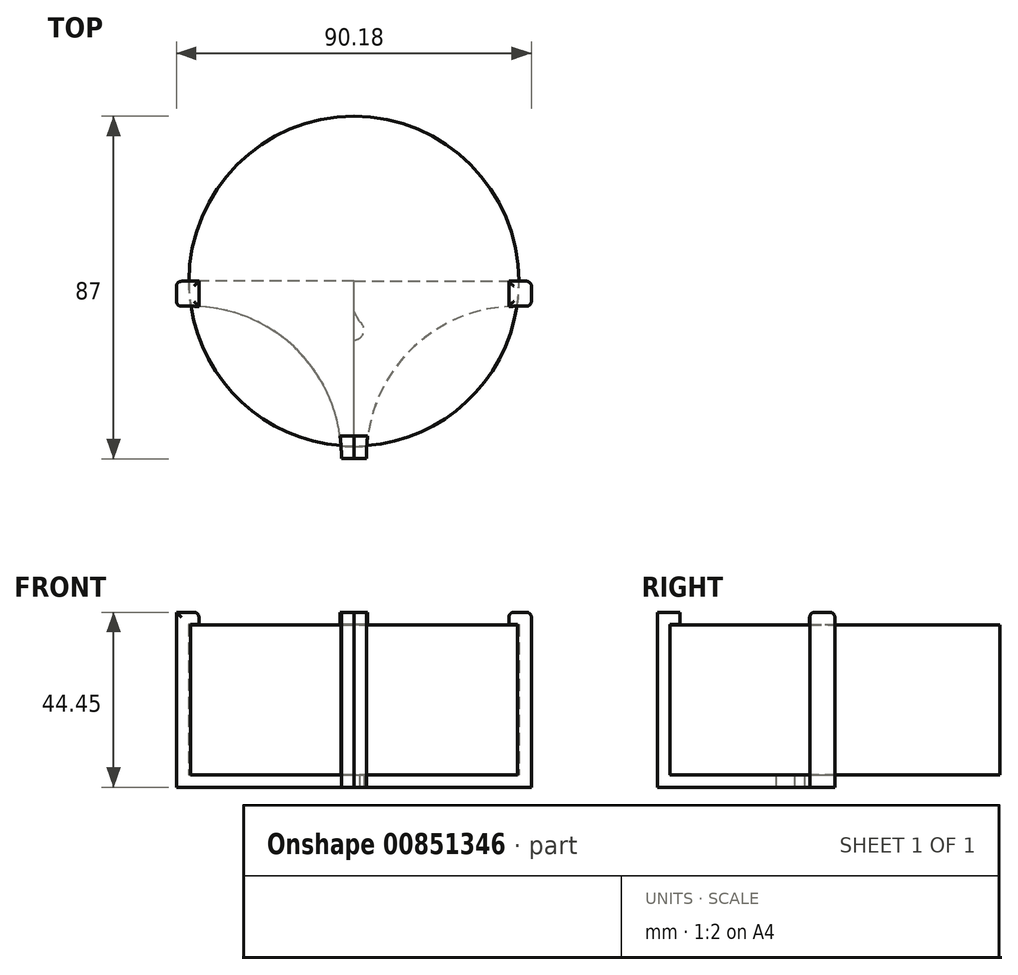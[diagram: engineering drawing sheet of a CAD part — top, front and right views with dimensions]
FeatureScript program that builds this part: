
annotation { "Feature Type Name" : "Feature", "Feature Type Description" : "" }
export const myFeature = defineFeature(function(context is Context, id is Id, definition is map)
    precondition{}
    {
        {
            var Q0;
            Q0=qCreatedBy(makeId("Top.planeOp"),FACE);
            var sketch = newSketch(context, id + "F0", { "sketchPlane" : qUnion([Q0])});
            skCircle(sketch, "E0", {"center": v(0, 0) * mm, "radius": 41.91 * mm});
            skSolve(sketch);
        }
        {
            var Q0;
            Q0=makeQuery(id+"F0.imprint","IMPRINT",FACE,{"disambiguationData":[TD([[makeQuery(id+"F0.imprint","IMPRINT",EDGE,{"derivedFrom":sQuery(id+"F0.wireOp",EDGE,"E0")}),1.0]])]});
            extrude(context, id + "F1", {"entities" : qUnion([Q0]), "depth" : 38.1 * mm, "offsetDistance" : 25.4 * mm});
        }
        {
            var Q0;
            Q0=qCreatedBy(makeId("Top.planeOp"),FACE);
            var sketch = newSketch(context, id + "F2", { "sketchPlane" : qUnion([Q0])});
            skLineSegment(sketch, "E1", {"start": v(0, 0) * mm, "end": v(45.09, 0) * mm});
            skLineSegment(sketch, "E2", {"start": v(45.09, 0) * mm, "end": v(45.09, -6.35) * mm});
            skLineSegment(sketch, "E3", {"start": v(45.08, -6.35) * mm, "end": v(41.27, -6.35) * mm});
            skLineSegment(sketch, "E4", {"start": v(3.18, -44.45) * mm, "end": v(3.18, -45.09) * mm});
            skLineSegment(sketch, "E5", {"start": v(3.18, -45.09) * mm, "end": v(0, -45.09) * mm});
            skLineSegment(sketch, "E6", {"start": v(0, -45.09) * mm, "end": v(0, 0) * mm});
            skPoint(sketch, "E7.visualSharp", {"position": v(3.17, -6.35) * mm});
            skArc(sketch, "E7.filletArc", {"start": v(41.27, -6.35) * mm, "mid": v(14.33, -17.5) * mm, "end": v(3.18, -44.45) * mm});
            skSolve(sketch);
        }
        {
            var Q0;
            Q0=makeQuery(id+"F2.imprint","IMPRINT",FACE,{"disambiguationData":[TD([[makeQuery(id+"F2.imprint","IMPRINT",EDGE,{"derivedFrom":sQuery(id+"F2.wireOp",EDGE,"E1")}),-1.0]])]});
            extrude(context, id + "F3", {"entities" : qUnion([Q0]), "depth" : 41.27 * mm, "offsetDistance" : 25.4 * mm, "hasSecondDirection" : true, "secondDirectionOppositeDirection" : true, "secondDirectionDepth" : 3.17 * mm});
        }
        {
            var Q0;
            Q0=makeQuery(id+"F1.opExtrude","SWEPT_BODY",BODY,{"disambiguationData":[OSD([sQuery(id+"F0.wireOp",EDGE,"E0")])]});
            var Q1;
            Q1=makeQuery(id+"F3.opExtrude","SWEPT_BODY",BODY,{"disambiguationData":[OSD([sQuery(id+"F2.wireOp",EDGE,"E1"),sQuery(id+"F2.wireOp",EDGE,"E2"),sQuery(id+"F2.wireOp",EDGE,"E3"),sQuery(id+"F2.wireOp",EDGE,"E4"),sQuery(id+"F2.wireOp",EDGE,"E5"),sQuery(id+"F2.wireOp",EDGE,"E6"),sQuery(id+"F2.wireOp",EDGE,"E7.filletArc")])]});
            var Q2;
            Q2=makeQuery(id+"F1.opExtrude","CAP_FACE",FACE,{"disambiguationData":[OSD([sQuery(id+"F0.wireOp",EDGE,"E0")])],"isStart":false});
            var Q3;
            Q3=makeQuery(id+"F1.opExtrude","SWEPT_FACE",FACE,{"disambiguationData":[OSD([sQuery(id+"F0.wireOp",EDGE,"E0")])]});
            var Q4;
            Q4=makeQuery(id+"F1.opExtrude","CAP_FACE",FACE,{"disambiguationData":[OSD([sQuery(id+"F0.wireOp",EDGE,"E0")])],"isStart":true});
            booleanBodies(context, id + "F4", {"operationType" : BooleanOperationType.SUBTRACTION, "tools" : qUnion([Q0]), "targets" : qUnion([Q1]), "offset" : true, "entitiesToOffset" : qUnion([Q2, Q3, Q4]), "offsetDistance" : 0.08 * mm, "keepTools" : true});
        }
        {
            var Q0;
            Q0=makeQuery(id+"F3.opExtrude","CAP_FACE",FACE,{"disambiguationData":[OSD([sQuery(id+"F2.wireOp",EDGE,"E1"),sQuery(id+"F2.wireOp",EDGE,"E2"),sQuery(id+"F2.wireOp",EDGE,"E3"),sQuery(id+"F2.wireOp",EDGE,"E4"),sQuery(id+"F2.wireOp",EDGE,"E5"),sQuery(id+"F2.wireOp",EDGE,"E6"),sQuery(id+"F2.wireOp",EDGE,"E7.filletArc")])],"isStart":false});
            var sketch = newSketch(context, id + "F5", { "sketchPlane" : qUnion([Q0])});
            skLineSegment(sketch, "E8.bottom", {"start": v(0, 10.15) * mm, "end": v(39.37, 10.15) * mm});
            skLineSegment(sketch, "E8.top", {"start": v(0, -39.37) * mm, "end": v(39.37, -39.37) * mm});
            skLineSegment(sketch, "E8.left", {"start": v(0, 10.15) * mm, "end": v(0, -39.37) * mm});
            skLineSegment(sketch, "E8.right", {"start": v(39.37, 10.15) * mm, "end": v(39.37, -39.37) * mm});
            skSolve(sketch);
        }
        {
            var Q0;
            {var subQ1=makeQuery(id+"F3.opExtrude","CAP_EDGE",EDGE,{"disambiguationData":[OSD([sQuery(id+"F2.wireOp",EDGE,"E1")])],"isStart":false});var subQ3=sQuery(id+"F5.wireOp",EDGE,"E8.right");var subQ4=makeQuery(id+"F5.imprint","INTERSECT",VERTEX,{"derivedFrom":[subQ1,subQ3]});Q0=makeQuery(id+"F5.imprint","IMPRINT",FACE,{"disambiguationData":[TD([[makeQuery(id+"F5.imprint","IMPRINT",EDGE,{"disambiguationData":[TD([[subQ4,-1.0]])],"derivedFrom":subQ3}),-1.0]])]});}
            extrude(context, id + "F6", {"entities" : qUnion([Q0]), "operationType" : NewBodyOperationType.REMOVE, "endBound" : BoundingType.UP_TO_NEXT, "oppositeDirection" : true, "depth" : 25.4 * mm, "offsetDistance" : 25.4 * mm});
        }
        {
            var Q0;
            Q0=makeQuery(id+"F3.opExtrude","SWEPT_BODY",BODY,{"disambiguationData":[OSD([sQuery(id+"F2.wireOp",EDGE,"E1"),sQuery(id+"F2.wireOp",EDGE,"E2"),sQuery(id+"F2.wireOp",EDGE,"E3"),sQuery(id+"F2.wireOp",EDGE,"E4"),sQuery(id+"F2.wireOp",EDGE,"E5"),sQuery(id+"F2.wireOp",EDGE,"E6"),sQuery(id+"F2.wireOp",EDGE,"E7.filletArc")])]});
            var Q1;
            Q1=makeQuery(id+"F3.opExtrude","SWEPT_FACE",FACE,{"disambiguationData":[OSD([sQuery(id+"F2.wireOp",EDGE,"E6")])]});
            mirror(context, id + "F7", {"operationType" : NewBodyOperationType.ADD, "entities" : qUnion([Q0]), "mirrorPlane" : qUnion([Q1])});
        }
        {
            var Q0;
            Q0=makeQuery(id+"F7.opPattern","COPY",EDGE,{"derivedFrom":makeQuery(id+"F3.opExtrude","SWEPT_EDGE",EDGE,{"disambiguationData":[OSD([sQuery(id+"F2.wireOp",EDGE,"E1"),sQuery(id+"F2.wireOp",EDGE,"E2")])]}),"instanceName":"1"});
            var Q1;
            Q1=makeQuery(id+"F7.opPattern","COPY",EDGE,{"derivedFrom":makeQuery(id+"F3.opExtrude","SWEPT_EDGE",EDGE,{"disambiguationData":[OSD([sQuery(id+"F2.wireOp",EDGE,"E2"),sQuery(id+"F2.wireOp",EDGE,"E3")])]}),"instanceName":"1"});
            var Q2;
            {var subQ0=sQuery(id+"F2.wireOp",EDGE,"E7.filletArc");var subQ1=sQuery(id+"F2.wireOp",EDGE,"E3");Q2=makeQuery(id+"F7.opPattern","COPY",EDGE,{"derivedFrom":makeQuery(id+"F6.boolean.opBoolean","SPLIT",EDGE,{"disambiguationData":[TD([makeQuery(id+"F3.opExtrude","SWEPT_FACE",FACE,{"disambiguationData":[OSD([subQ1])]})])],"derivedFrom":makeQuery(id+"F3.opExtrude","CAP_EDGE",EDGE,{"disambiguationData":[OSD([subQ0])],"isStart":false})}),"instanceName":"1"});}
            var Q3;
            Q3=makeQuery(id+"F7.opPattern","COPY",EDGE,{"derivedFrom":makeQuery(id+"F6.boolean.opBoolean","COPY",EDGE,{"derivedFrom":makeQuery(id+"F6.opExtrude","CAP_EDGE",EDGE,{"disambiguationData":[OSD([sQuery(id+"F5.wireOp",EDGE,"E8.right")])],"isStart":true})}),"instanceName":"1"});
            var Q4;
            Q4=makeQuery(id+"F3.opExtrude","CAP_EDGE",EDGE,{"disambiguationData":[OSD([sQuery(id+"F2.wireOp",EDGE,"E1")])],"isStart":false});
            var Q5;
            Q5=makeQuery(id+"F3.opExtrude","CAP_EDGE",EDGE,{"disambiguationData":[OSD([sQuery(id+"F2.wireOp",EDGE,"E2")])],"isStart":false});
            var Q6;
            Q6=makeQuery(id+"F3.opExtrude","CAP_EDGE",EDGE,{"disambiguationData":[OSD([sQuery(id+"F2.wireOp",EDGE,"E3")])],"isStart":false});
            var Q7;
            Q7=makeQuery(id+"F6.boolean.opBoolean","COPY",EDGE,{"derivedFrom":makeQuery(id+"F6.opExtrude","CAP_EDGE",EDGE,{"disambiguationData":[OSD([sQuery(id+"F5.wireOp",EDGE,"E8.right")])],"isStart":true})});
            var Q8;
            Q8=makeQuery(id+"F6.boolean.opBoolean","COPY",EDGE,{"derivedFrom":makeQuery(id+"F6.opExtrude","SWEPT_EDGE",EDGE,{"disambiguationData":[OSD([sQuery(id+"F2.wireOp",EDGE,"E1"),sQuery(id+"F5.wireOp",EDGE,"E8.right")])]})});
            var Q9;
            Q9=makeQuery(id+"F6.boolean.opBoolean","COPY",EDGE,{"derivedFrom":makeQuery(id+"F6.opExtrude","SWEPT_EDGE",EDGE,{"disambiguationData":[OSD([sQuery(id+"F2.wireOp",EDGE,"E7.filletArc"),sQuery(id+"F5.wireOp",EDGE,"E8.right")])]})});
            var Q10;
            Q10=makeQuery(id+"F3.opExtrude","SWEPT_EDGE",EDGE,{"disambiguationData":[OSD([sQuery(id+"F2.wireOp",EDGE,"E1"),sQuery(id+"F2.wireOp",EDGE,"E2")])]});
            var Q11;
            Q11=makeQuery(id+"F3.opExtrude","SWEPT_EDGE",EDGE,{"disambiguationData":[OSD([sQuery(id+"F2.wireOp",EDGE,"E2"),sQuery(id+"F2.wireOp",EDGE,"E3")])]});
            var Q12;
            Q12=makeQuery(id+"F7.opPattern","COPY",EDGE,{"derivedFrom":makeQuery(id+"F3.opExtrude","CAP_EDGE",EDGE,{"disambiguationData":[OSD([sQuery(id+"F2.wireOp",EDGE,"E1")])],"isStart":false}),"instanceName":"1"});
            var Q13;
            Q13=makeQuery(id+"F7.opPattern","COPY",EDGE,{"derivedFrom":makeQuery(id+"F6.boolean.opBoolean","COPY",EDGE,{"derivedFrom":makeQuery(id+"F6.opExtrude","SWEPT_EDGE",EDGE,{"disambiguationData":[OSD([sQuery(id+"F2.wireOp",EDGE,"E1"),sQuery(id+"F5.wireOp",EDGE,"E8.right")])]})}),"instanceName":"1"});
            var Q14;
            Q14=makeQuery(id+"F7.opPattern","COPY",EDGE,{"derivedFrom":makeQuery(id+"F6.boolean.opBoolean","COPY",EDGE,{"derivedFrom":makeQuery(id+"F6.opExtrude","SWEPT_EDGE",EDGE,{"disambiguationData":[OSD([sQuery(id+"F2.wireOp",EDGE,"E7.filletArc"),sQuery(id+"F5.wireOp",EDGE,"E8.right")])]})}),"instanceName":"1"});
            fillet(context, id + "F8", {"entities" : qUnion([Q0, Q1, Q2, Q3, Q4, Q5, Q6, Q7, Q8, Q9, Q10, Q11, Q12, Q13, Q14]), "radius" : 1.27 * mm, "tangentPropagation" : true, "allowEdgeOverflow" : false});
        }
        {
            var Q0;
            {var subQ0=makeQuery(id+"F3.opExtrude","CAP_FACE",FACE,{"disambiguationData":[OSD([sQuery(id+"F2.wireOp",EDGE,"E1"),sQuery(id+"F2.wireOp",EDGE,"E2"),sQuery(id+"F2.wireOp",EDGE,"E3"),sQuery(id+"F2.wireOp",EDGE,"E4"),sQuery(id+"F2.wireOp",EDGE,"E5"),sQuery(id+"F2.wireOp",EDGE,"E6"),sQuery(id+"F2.wireOp",EDGE,"E7.filletArc")])],"isStart":true});Q0=makeQuery(id+"F7.boolean.opBoolean","MERGE",FACE,{"derivedFrom":[subQ0,makeQuery(id+"F7.opPattern","COPY",FACE,{"derivedFrom":subQ0,"instanceName":"1"})]});}
            var sketch = newSketch(context, id + "F9", { "sketchPlane" : qUnion([Q0])});
            skCircle(sketch, "E9", {"center": v(0, 12.38) * mm, "radius": 2.54 * mm});
            skSolve(sketch);
        }
        {
            var Q0;
            Q0=makeQuery(id+"F9.imprint","IMPRINT",FACE,{"disambiguationData":[TD([[makeQuery(id+"F9.imprint","IMPRINT",EDGE,{"derivedFrom":sQuery(id+"F9.wireOp",EDGE,"E9")}),1.0]])]});
            extrude(context, id + "F10", {"entities" : qUnion([Q0]), "operationType" : NewBodyOperationType.REMOVE, "endBound" : BoundingType.UP_TO_NEXT, "oppositeDirection" : true, "depth" : 25.4 * mm, "offsetDistance" : 25.4 * mm});
        }
        {
            var Q0;
            Q0=makeQuery(id+"F10.boolean.opBoolean","COPY",EDGE,{"derivedFrom":makeQuery(id+"F10.opExtrude","CAP_EDGE",EDGE,{"disambiguationData":[OSD([sQuery(id+"F9.wireOp",EDGE,"E9")])],"isStart":false})});
            chamfer(context, id + "F11", {"entities" : qUnion([Q0]), "width" : 3.17 * mm, "tangentPropagation" : true});
        }
    });
